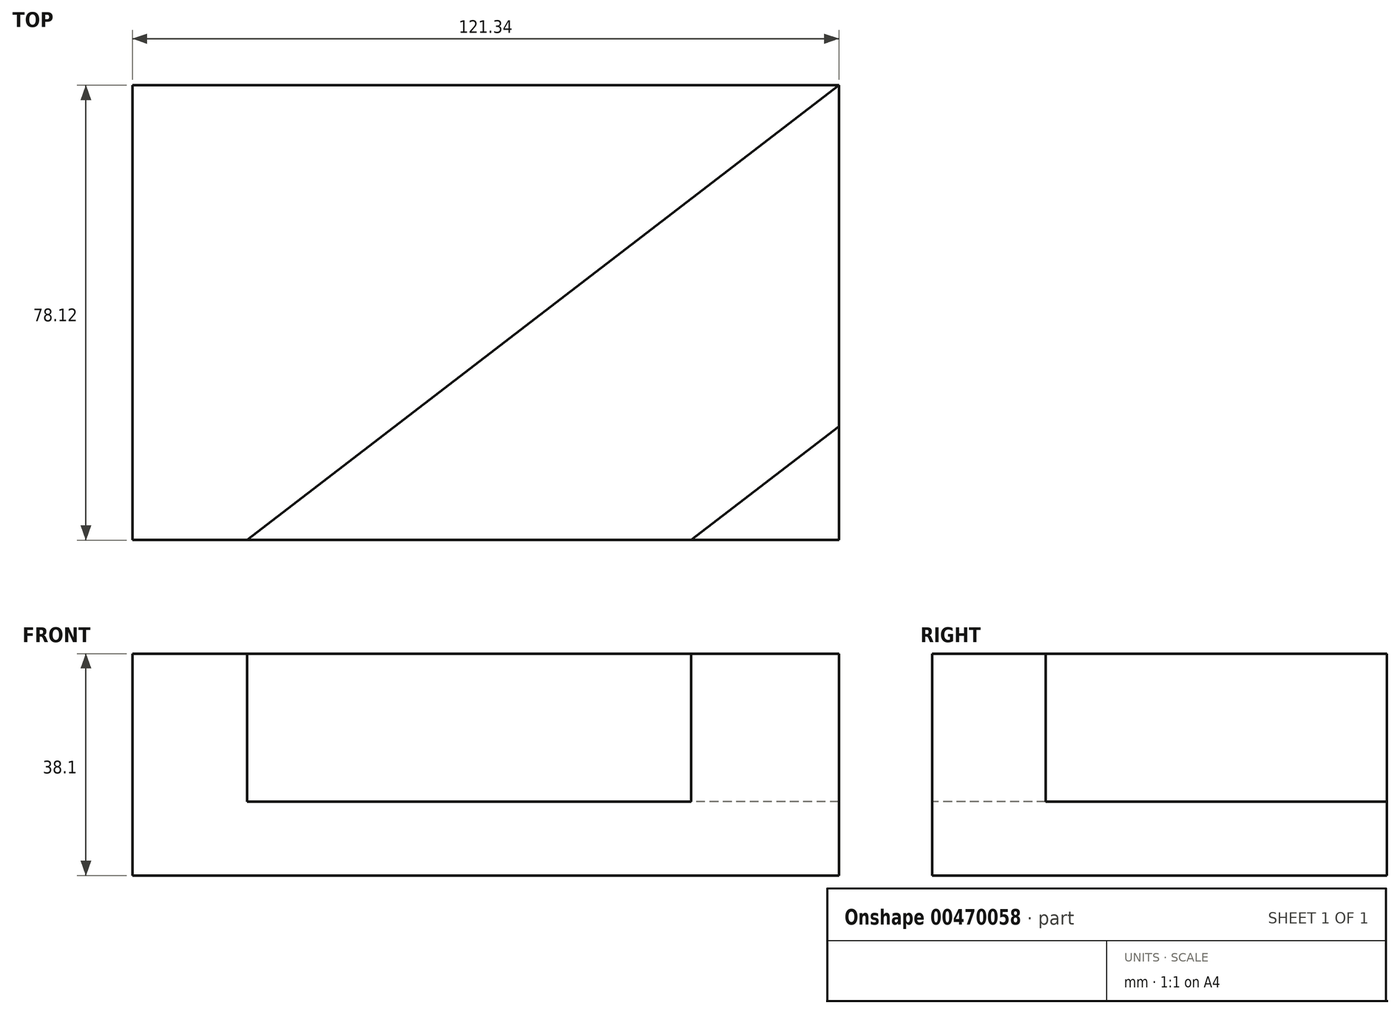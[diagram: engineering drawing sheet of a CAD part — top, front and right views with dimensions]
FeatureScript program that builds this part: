
annotation { "Feature Type Name" : "Feature", "Feature Type Description" : "" }
export const myFeature = defineFeature(function(context is Context, id is Id, definition is map)
    precondition{}
    {
        {
            var Q0;
            Q0=qCreatedBy(makeId("Top.planeOp"),FACE);
            var sketch = newSketch(context, id + "F0", { "sketchPlane" : qUnion([Q0])});
            skLineSegment(sketch, "E0.bottom", {"start": v(60.67, 39.06) * mm, "end": v(-60.67, 39.06) * mm});
            skLineSegment(sketch, "E0.top", {"start": v(60.67, -39.06) * mm, "end": v(-60.67, -39.06) * mm});
            skLineSegment(sketch, "E0.left", {"start": v(60.67, 39.06) * mm, "end": v(60.67, -39.06) * mm});
            skLineSegment(sketch, "E0.right", {"start": v(-60.67, 39.06) * mm, "end": v(-60.67, -39.06) * mm});
            skPoint(sketch, "E0.middle", {"position": v(0, 0) * mm});
            skLineSegment(sketch, "E1", {"start": v(60.67, -19.53) * mm, "end": v(35.27, -39.06) * mm});
            skLineSegment(sketch, "E2", {"start": v(60.67, 39.06) * mm, "end": v(-40.95, -39.06) * mm});
            skSolve(sketch);
        }
        {
            var Q0;
            {var subQ0=sQuery(id+"F0.wireOp",EDGE,"E1");Q0=makeQuery(id+"F0.imprint","IMPRINT",FACE,{"disambiguationData":[TD([[makeQuery(id+"F0.imprint","IMPRINT",EDGE,{"derivedFrom":subQ0}),-1.0]])]});}
            extrude(context, id + "F1", {"entities" : qUnion([Q0]), "depth" : 12.7 * mm});
        }
        {
            var Q0;
            {var subQ3=sQuery(id+"F0.wireOp",EDGE,"E1");Q0=makeQuery(id+"F0.imprint","IMPRINT",FACE,{"disambiguationData":[TD([[makeQuery(id+"F0.imprint","IMPRINT",EDGE,{"derivedFrom":subQ3}),1.0]])]});}
            extrude(context, id + "F2", {"entities" : qUnion([Q0]), "operationType" : NewBodyOperationType.ADD, "depth" : 38.1 * mm});
        }
        {
            var Q0;
            Q0=makeQuery(id+"F0.imprint","IMPRINT",FACE,{"disambiguationData":[TD([[makeQuery(id+"F0.imprint","IMPRINT",EDGE,{"derivedFrom":sQuery(id+"F0.wireOp",EDGE,"E0.bottom")}),1.0]])]});
            extrude(context, id + "F3", {"entities" : qUnion([Q0]), "operationType" : NewBodyOperationType.ADD, "depth" : 38.1 * mm});
        }
    });
